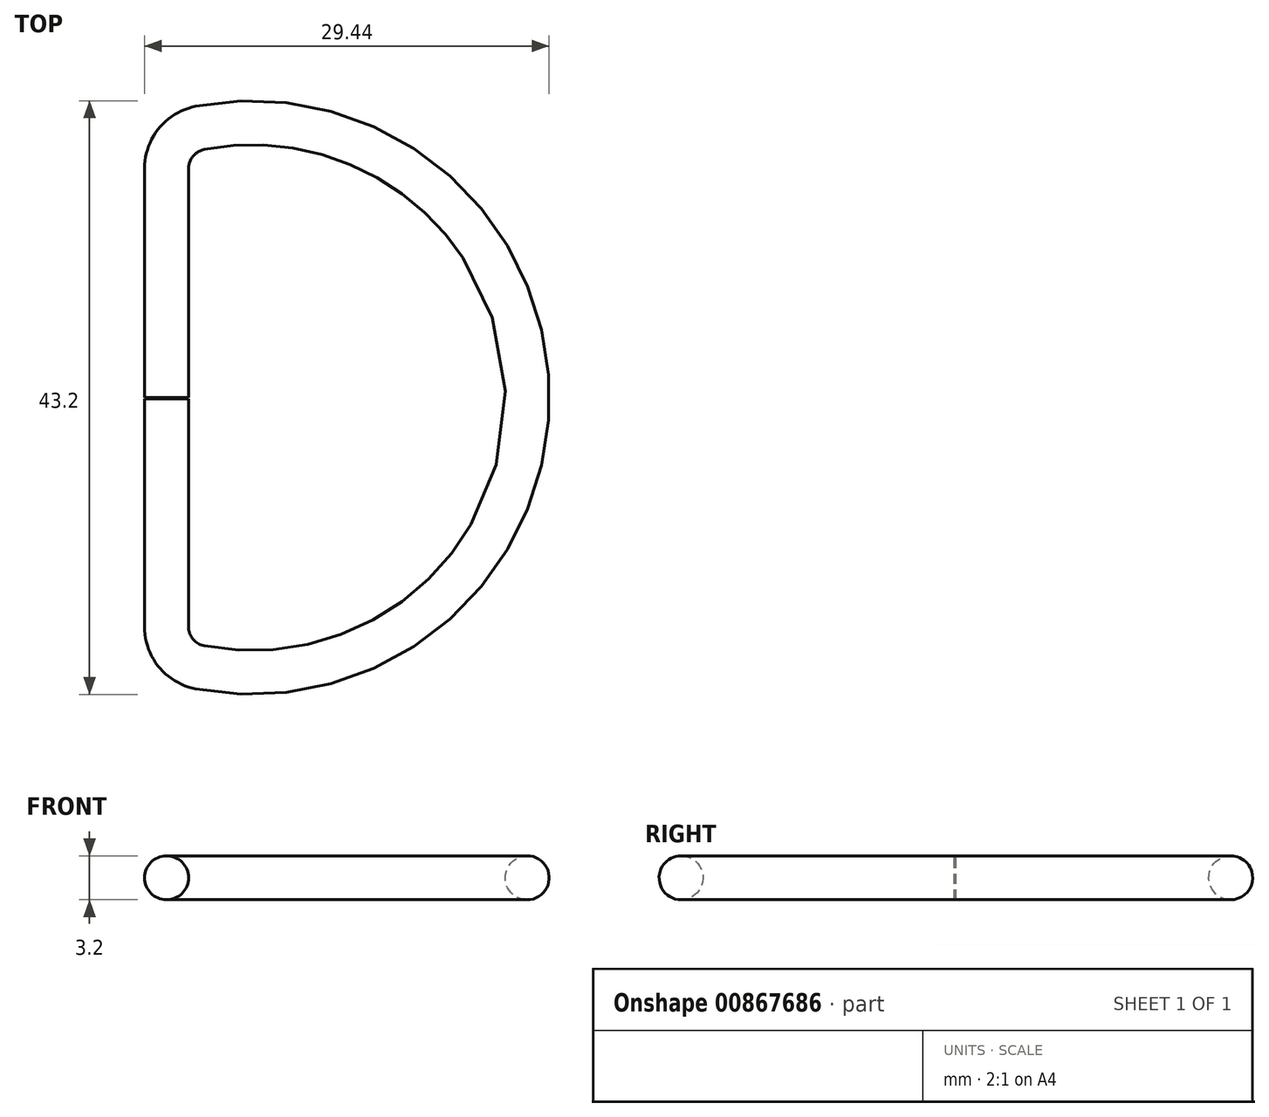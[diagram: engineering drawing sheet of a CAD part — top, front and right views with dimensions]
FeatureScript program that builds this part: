
annotation { "Feature Type Name" : "Feature", "Feature Type Description" : "" }
export const myFeature = defineFeature(function(context is Context, id is Id, definition is map)
    precondition{}
    {
        {
            var Q0;
            Q0=qCreatedBy(makeId("Top.planeOp"),FACE);
            var sketch = newSketch(context, id + "F0", { "sketchPlane" : qUnion([Q0])});
            skLineSegment(sketch, "E0", {"start": v(0, 0) * mm, "end": v(0, 16.69) * mm});
            skPoint(sketch, "E1", {"position": v(0, -19) * mm});
            skArc(sketch, "E2", {"start": v(2.43, -19.63) * mm, "mid": v(26.24, 0) * mm, "end": v(2.43, 19.63) * mm});
            skLineSegment(sketch, "E3", {"start": v(0, -16.69) * mm, "end": v(0, -0.1) * mm});
            skPoint(sketch, "E4.visualSharp", {"position": v(0, 19) * mm});
            skArc(sketch, "E4.filletArc", {"start": v(2.43, 19.63) * mm, "mid": v(0.69, 18.6) * mm, "end": v(0, 16.69) * mm});
            skArc(sketch, "E5.filletArc", {"start": v(0, -16.69) * mm, "mid": v(0.69, -18.6) * mm, "end": v(2.43, -19.63) * mm});
            skSolve(sketch);
        }
        {
            var Q0;
            Q0=qCreatedBy(makeId("Front.planeOp"),FACE);
            var sketch = newSketch(context, id + "F1", { "sketchPlane" : qUnion([Q0])});
            skCircle(sketch, "E6", {"center": v(0, 0) * mm, "radius": 1.6 * mm});
            skSolve(sketch);
        }
        {
            var Q0;
            Q0 = qSketchRegion(id + "F1", true);
            var Q1;
            Q1 = qConstructionFilter(qBodyType(qCreatedBy(id + "F0" ,EDGE), BodyType.WIRE), ConstructionObject.NO);
            sweep(context, id + "F2", {"profiles" : qUnion([Q0]), "path" : qUnion([Q1])});
        }
    });
